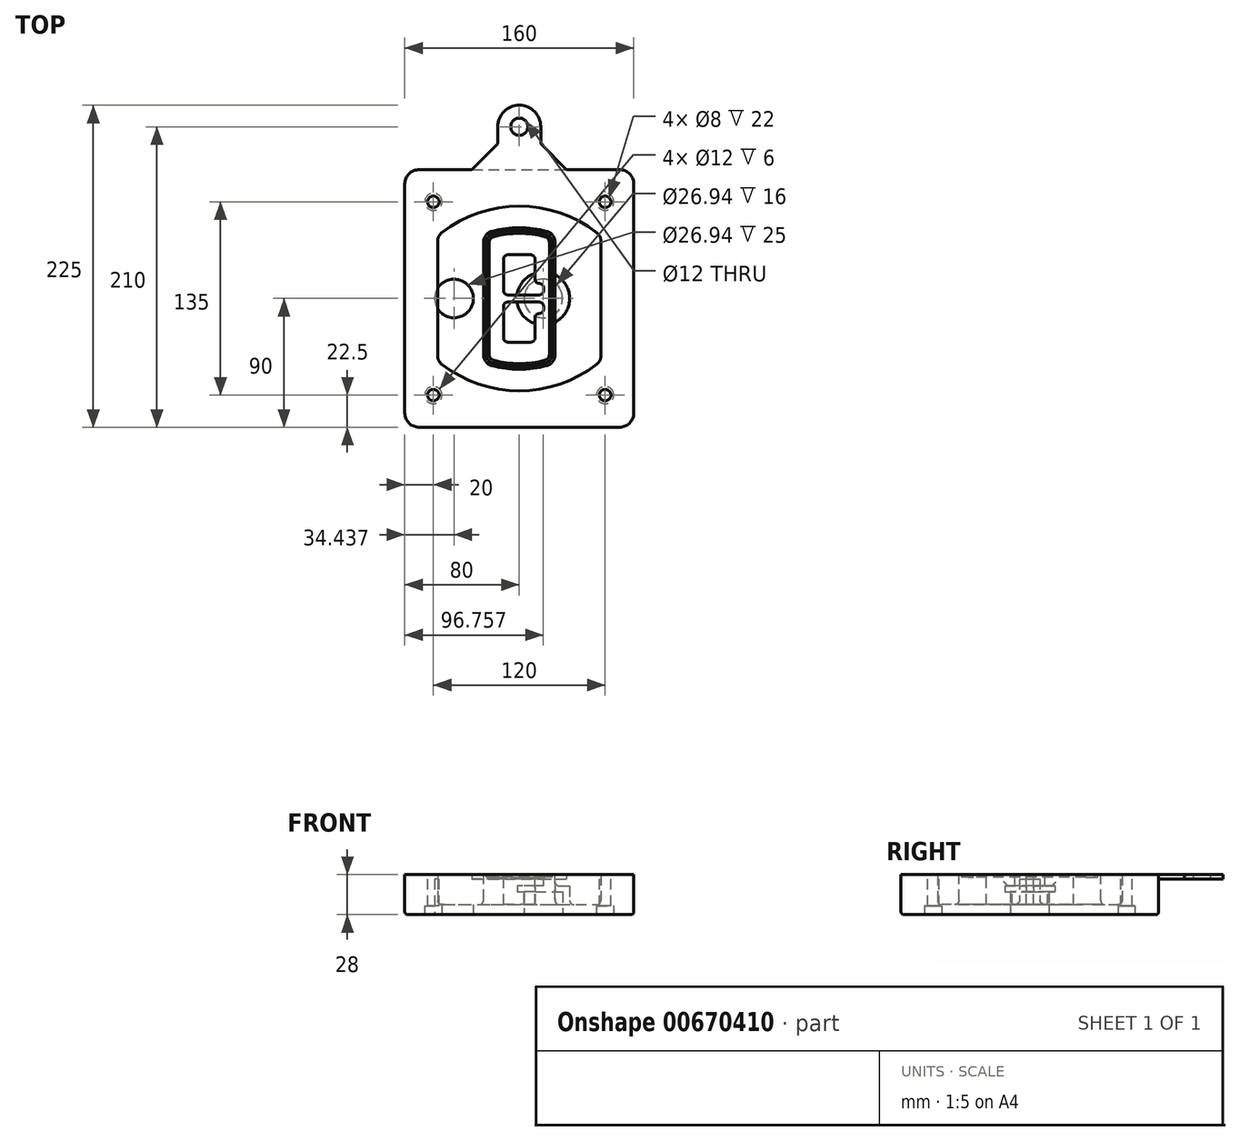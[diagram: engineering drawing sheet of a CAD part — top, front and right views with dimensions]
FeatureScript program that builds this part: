
annotation { "Feature Type Name" : "Feature", "Feature Type Description" : "" }
export const myFeature = defineFeature(function(context is Context, id is Id, definition is map)
    precondition{}
    {
        {
            var Q0;
            Q0=qCreatedBy(makeId("Top.planeOp"),FACE);
            var sketch = newSketch(context, id + "F0", { "sketchPlane" : qUnion([Q0])});
            skPoint(sketch, "E0.rect.middle", {"position": v(0, 0) * mm});
            skLineSegment(sketch, "E1.bottom", {"start": v(-70, -90) * mm, "end": v(70, -90) * mm});
            skLineSegment(sketch, "E1.top", {"start": v(-70, 90) * mm, "end": v(70, 90) * mm});
            skLineSegment(sketch, "E1.left", {"start": v(-80, -80) * mm, "end": v(-80, 80) * mm});
            skLineSegment(sketch, "E1.right", {"start": v(80, -80) * mm, "end": v(80, 80) * mm});
            skLineSegment(sketch, "E2", {"start": v(-80, 90) * mm, "end": v(80, -90) * mm, "construction": true});
            skLineSegment(sketch, "E3", {"start": v(80, 90) * mm, "end": v(-80, -90) * mm, "construction": true});
            skCircle(sketch, "E4", {"center": v(-60, 67.5) * mm, "radius": 4 * mm});
            skCircle(sketch, "E5", {"center": v(60, 67.5) * mm, "radius": 4 * mm});
            skCircle(sketch, "E6", {"center": v(60, -67.5) * mm, "radius": 4 * mm});
            skCircle(sketch, "E7", {"center": v(-60, -67.5) * mm, "radius": 4 * mm});
            skLineSegment(sketch, "E8", {"start": v(-60, 67.5) * mm, "end": v(60, 67.5) * mm, "construction": true});
            skLineSegment(sketch, "E9", {"start": v(60, 67.5) * mm, "end": v(60, -67.5) * mm, "construction": true});
            skLineSegment(sketch, "E10", {"start": v(60, -67.5) * mm, "end": v(-60, -67.5) * mm, "construction": true});
            skLineSegment(sketch, "E11", {"start": v(-60, -67.5) * mm, "end": v(-60, 67.5) * mm, "construction": true});
            skLineSegment(sketch, "E12", {"start": v(-60, 40.3) * mm, "end": v(-60, -40.3) * mm});
            skLineSegment(sketch, "E13", {"start": v(60, 40.3) * mm, "end": v(60, -40.3) * mm});
            skArc(sketch, "E14", {"start": v(56.15, 48.18) * mm, "mid": v(0, 67.5) * mm, "end": v(-56.15, 48.18) * mm});
            skArc(sketch, "E15", {"start": v(-56.15, -48.18) * mm, "mid": v(0, -67.5) * mm, "end": v(56.15, -48.18) * mm});
            skLineSegment(sketch, "E16", {"start": v(-60, 0) * mm, "end": v(60, 0) * mm, "construction": true});
            skPoint(sketch, "E17.visualSharp", {"position": v(-60, -45) * mm});
            skArc(sketch, "E17.filletArc", {"start": v(-60, -40.3) * mm, "mid": v(-58.99, -44.68) * mm, "end": v(-56.15, -48.18) * mm});
            skPoint(sketch, "E18.visualSharp", {"position": v(-60, 45) * mm});
            skArc(sketch, "E18.filletArc", {"start": v(-56.15, 48.18) * mm, "mid": v(-58.99, 44.68) * mm, "end": v(-60, 40.3) * mm});
            skPoint(sketch, "E19.visualSharp", {"position": v(60, 45) * mm});
            skArc(sketch, "E19.filletArc", {"start": v(60, 40.3) * mm, "mid": v(58.99, 44.68) * mm, "end": v(56.15, 48.18) * mm});
            skPoint(sketch, "E20.visualSharp", {"position": v(60, -45) * mm});
            skArc(sketch, "E20.filletArc", {"start": v(56.15, -48.18) * mm, "mid": v(58.99, -44.68) * mm, "end": v(60, -40.3) * mm});
            skPoint(sketch, "E21.visualSharp", {"position": v(-80, 90) * mm});
            skArc(sketch, "E21.filletArc", {"start": v(-70, 90) * mm, "mid": v(-77.07, 87.07) * mm, "end": v(-80, 80) * mm});
            skPoint(sketch, "E22.visualSharp", {"position": v(80, 90) * mm});
            skArc(sketch, "E22.filletArc", {"start": v(80, 80) * mm, "mid": v(77.07, 87.07) * mm, "end": v(70, 90) * mm});
            skPoint(sketch, "E23.visualSharp", {"position": v(80, -90) * mm});
            skArc(sketch, "E23.filletArc", {"start": v(70, -90) * mm, "mid": v(77.07, -87.07) * mm, "end": v(80, -80) * mm});
            skPoint(sketch, "E24.visualSharp", {"position": v(-80, -90) * mm});
            skArc(sketch, "E24.filletArc", {"start": v(-80, -80) * mm, "mid": v(-77.07, -87.07) * mm, "end": v(-70, -90) * mm});
            skArc(sketch, "E25.0", {"start": v(57, 40.3) * mm, "mid": v(56.3, 43.36) * mm, "end": v(54.3, 45.81) * mm});
            skLineSegment(sketch, "E25.1", {"start": v(57, 40.3) * mm, "end": v(57, -40.3) * mm});
            skArc(sketch, "E25.2", {"start": v(54.3, -45.81) * mm, "mid": v(56.3, -43.36) * mm, "end": v(57, -40.3) * mm});
            skArc(sketch, "E25.3", {"start": v(-54.3, -45.81) * mm, "mid": v(0, -64.5) * mm, "end": v(54.3, -45.81) * mm});
            skArc(sketch, "E25.4", {"start": v(-57, -40.3) * mm, "mid": v(-56.3, -43.36) * mm, "end": v(-54.3, -45.81) * mm});
            skArc(sketch, "E25.5", {"start": v(54.3, 45.81) * mm, "mid": v(0, 64.5) * mm, "end": v(-54.3, 45.81) * mm});
            skLineSegment(sketch, "E25.6", {"start": v(-57, 40.3) * mm, "end": v(-57, -40.3) * mm});
            skArc(sketch, "E25.7", {"start": v(-54.3, 45.81) * mm, "mid": v(-56.3, 43.36) * mm, "end": v(-57, 40.3) * mm});
            skArc(sketch, "E26.0", {"start": v(-58.62, 51.33) * mm, "mid": v(-62.58, 46.43) * mm, "end": v(-64, 40.3) * mm});
            skArc(sketch, "E26.1", {"start": v(58.62, 51.33) * mm, "mid": v(0, 71.5) * mm, "end": v(-58.62, 51.33) * mm});
            skArc(sketch, "E26.2", {"start": v(64, 40.3) * mm, "mid": v(62.58, 46.43) * mm, "end": v(58.62, 51.33) * mm});
            skLineSegment(sketch, "E26.3", {"start": v(64, 40.3) * mm, "end": v(64, -40.3) * mm});
            skArc(sketch, "E26.4", {"start": v(58.62, -51.33) * mm, "mid": v(62.58, -46.43) * mm, "end": v(64, -40.3) * mm});
            skLineSegment(sketch, "E26.5", {"start": v(-64, 40.3) * mm, "end": v(-64, -40.3) * mm});
            skArc(sketch, "E26.6", {"start": v(-58.62, -51.33) * mm, "mid": v(0, -71.5) * mm, "end": v(58.62, -51.33) * mm});
            skArc(sketch, "E26.7", {"start": v(-64, -40.3) * mm, "mid": v(-62.58, -46.43) * mm, "end": v(-58.62, -51.33) * mm});
            skSolve(sketch);
        }
        {
            var Q0;
            Q0=makeQuery(id+"F0.imprint","IMPRINT",FACE,{"disambiguationData":[TD([[makeQuery(id+"F0.imprint","IMPRINT",EDGE,{"derivedFrom":sQuery(id+"F0.wireOp",EDGE,"E1.bottom")}),1.0]])]});
            var Q1;
            Q1=makeQuery(id+"F0.imprint","IMPRINT",FACE,{"disambiguationData":[TD([[makeQuery(id+"F0.imprint","IMPRINT",EDGE,{"derivedFrom":sQuery(id+"F0.wireOp",EDGE,"E12")}),1.0]])]});
            var Q2;
            Q2=makeQuery(id+"F0.imprint","IMPRINT",FACE,{"disambiguationData":[TD([[makeQuery(id+"F0.imprint","IMPRINT",EDGE,{"derivedFrom":sQuery(id+"F0.wireOp",EDGE,"E25.0")}),1.0]])]});
            var Q3;
            Q3=makeQuery(id+"F0.imprint","IMPRINT",FACE,{"disambiguationData":[TD([[makeQuery(id+"F0.imprint","IMPRINT",EDGE,{"derivedFrom":sQuery(id+"F0.wireOp",EDGE,"E12")}),-1.0]])]});
            extrude(context, id + "F1", {"entities" : qUnion([Q0, Q1, Q2, Q3]), "oppositeDirection" : true, "depth" : 25 * mm});
        }
        {
            var Q0;
            Q0=makeQuery(id+"F0.imprint","IMPRINT",FACE,{"disambiguationData":[TD([[makeQuery(id+"F0.imprint","IMPRINT",EDGE,{"derivedFrom":sQuery(id+"F0.wireOp",EDGE,"E12")}),1.0]])]});
            extrude(context, id + "F2", {"entities" : qUnion([Q0]), "operationType" : NewBodyOperationType.ADD, "depth" : 3 * mm});
        }
        {
            var Q0;
            Q0=makeQuery(id+"F0.imprint","IMPRINT",FACE,{"disambiguationData":[TD([[makeQuery(id+"F0.imprint","IMPRINT",EDGE,{"derivedFrom":sQuery(id+"F0.wireOp",EDGE,"E25.0")}),1.0]])]});
            extrude(context, id + "F3", {"entities" : qUnion([Q0]), "operationType" : NewBodyOperationType.REMOVE, "oppositeDirection" : true, "depth" : 18 * mm});
        }
        {
            var Q0;
            Q0=makeQuery(id+"F2.opExtrude","CAP_FACE",FACE,{"disambiguationData":[OSD([sQuery(id+"F0.wireOp",EDGE,"E12"),sQuery(id+"F0.wireOp",EDGE,"E13"),sQuery(id+"F0.wireOp",EDGE,"E14"),sQuery(id+"F0.wireOp",EDGE,"E15"),sQuery(id+"F0.wireOp",EDGE,"E17.filletArc"),sQuery(id+"F0.wireOp",EDGE,"E18.filletArc"),sQuery(id+"F0.wireOp",EDGE,"E19.filletArc"),sQuery(id+"F0.wireOp",EDGE,"E20.filletArc"),sQuery(id+"F0.wireOp",EDGE,"E25.0"),sQuery(id+"F0.wireOp",EDGE,"E25.1"),sQuery(id+"F0.wireOp",EDGE,"E25.2"),sQuery(id+"F0.wireOp",EDGE,"E25.3"),sQuery(id+"F0.wireOp",EDGE,"E25.4"),sQuery(id+"F0.wireOp",EDGE,"E25.5"),sQuery(id+"F0.wireOp",EDGE,"E25.6"),sQuery(id+"F0.wireOp",EDGE,"E25.7")])],"isStart":false});
            var sketch = newSketch(context, id + "F4", { "sketchPlane" : qUnion([Q0])});
            skArc(sketch, "E27.0", {"start": v(-19.08, -46.97) * mm, "mid": v(0, -49.5) * mm, "end": v(19.08, -46.97) * mm});
            skArc(sketch, "E28.0", {"start": v(19.08, 46.97) * mm, "mid": v(0, 49.5) * mm, "end": v(-19.08, 46.97) * mm});
            skLineSegment(sketch, "E29", {"start": v(-25, 39.25) * mm, "end": v(-25, -39.25) * mm});
            skLineSegment(sketch, "E30", {"start": v(25, 39.25) * mm, "end": v(25, -39.25) * mm});
            skLineSegment(sketch, "E31", {"start": v(-25, 45.1) * mm, "end": v(25, 45.1) * mm, "construction": true});
            skLineSegment(sketch, "E32", {"start": v(-25, -45.1) * mm, "end": v(25, -45.1) * mm, "construction": true});
            skPoint(sketch, "E33.visualSharp", {"position": v(-25, 45.1) * mm});
            skArc(sketch, "E33.filletArc", {"start": v(-19.08, 46.97) * mm, "mid": v(-23.35, 44.11) * mm, "end": v(-25, 39.25) * mm});
            skPoint(sketch, "E34.visualSharp", {"position": v(25, 45.1) * mm});
            skArc(sketch, "E34.filletArc", {"start": v(25, 39.25) * mm, "mid": v(23.35, 44.11) * mm, "end": v(19.08, 46.97) * mm});
            skPoint(sketch, "E35.visualSharp", {"position": v(25, -45.1) * mm});
            skArc(sketch, "E35.filletArc", {"start": v(19.08, -46.97) * mm, "mid": v(23.35, -44.11) * mm, "end": v(25, -39.25) * mm});
            skPoint(sketch, "E36.visualSharp", {"position": v(-25, -45.1) * mm});
            skArc(sketch, "E36.filletArc", {"start": v(-25, -39.25) * mm, "mid": v(-23.35, -44.11) * mm, "end": v(-19.08, -46.97) * mm});
            skArc(sketch, "E37.0", {"start": v(54.3, 45.81) * mm, "mid": v(0, 64.5) * mm, "end": v(-54.3, 45.81) * mm});
            skArc(sketch, "E37.1", {"start": v(-54.3, 45.81) * mm, "mid": v(-56.3, 43.36) * mm, "end": v(-57, 40.3) * mm});
            skLineSegment(sketch, "E37.2", {"start": v(-57, 40.3) * mm, "end": v(-57, -40.3) * mm});
            skArc(sketch, "E37.3", {"start": v(-57, -40.3) * mm, "mid": v(-56.3, -43.36) * mm, "end": v(-54.3, -45.81) * mm});
            skArc(sketch, "E37.4", {"start": v(-54.3, -45.81) * mm, "mid": v(0, -64.5) * mm, "end": v(54.3, -45.81) * mm});
            skArc(sketch, "E37.5", {"start": v(54.3, -45.81) * mm, "mid": v(56.3, -43.36) * mm, "end": v(57, -40.3) * mm});
            skLineSegment(sketch, "E37.6", {"start": v(57, 40.3) * mm, "end": v(57, -40.3) * mm});
            skArc(sketch, "E37.7", {"start": v(57, 40.3) * mm, "mid": v(56.3, 43.36) * mm, "end": v(54.3, 45.81) * mm});
            skLineSegment(sketch, "E38.0", {"start": v(23, 39.25) * mm, "end": v(23, -39.25) * mm});
            skArc(sketch, "E38.1", {"start": v(18.56, -45.04) * mm, "mid": v(21.76, -42.9) * mm, "end": v(23, -39.25) * mm});
            skArc(sketch, "E38.2", {"start": v(-18.56, -45.04) * mm, "mid": v(0, -47.5) * mm, "end": v(18.56, -45.04) * mm});
            skArc(sketch, "E38.3", {"start": v(-23, -39.25) * mm, "mid": v(-21.76, -42.9) * mm, "end": v(-18.56, -45.04) * mm});
            skLineSegment(sketch, "E38.4", {"start": v(-23, 39.25) * mm, "end": v(-23, -39.25) * mm});
            skArc(sketch, "E38.5", {"start": v(23, 39.25) * mm, "mid": v(21.76, 42.9) * mm, "end": v(18.56, 45.04) * mm});
            skArc(sketch, "E38.6", {"start": v(-18.56, 45.04) * mm, "mid": v(-21.76, 42.9) * mm, "end": v(-23, 39.25) * mm});
            skArc(sketch, "E38.7", {"start": v(18.56, 45.04) * mm, "mid": v(0, 47.5) * mm, "end": v(-18.56, 45.04) * mm});
            skArc(sketch, "E39.0", {"start": v(21, 39.25) * mm, "mid": v(20.18, 41.68) * mm, "end": v(18.04, 43.1) * mm});
            skLineSegment(sketch, "E39.1", {"start": v(21, 39.25) * mm, "end": v(21, -39.25) * mm});
            skArc(sketch, "E39.2", {"start": v(18.04, -43.1) * mm, "mid": v(20.18, -41.68) * mm, "end": v(21, -39.25) * mm});
            skArc(sketch, "E39.3", {"start": v(-18.04, -43.1) * mm, "mid": v(0, -45.5) * mm, "end": v(18.04, -43.1) * mm});
            skArc(sketch, "E39.4", {"start": v(-21, -39.25) * mm, "mid": v(-20.18, -41.68) * mm, "end": v(-18.04, -43.1) * mm});
            skArc(sketch, "E39.5", {"start": v(18.04, 43.1) * mm, "mid": v(0, 45.5) * mm, "end": v(-18.04, 43.1) * mm});
            skLineSegment(sketch, "E39.6", {"start": v(-21, 39.25) * mm, "end": v(-21, -39.25) * mm});
            skArc(sketch, "E39.7", {"start": v(-18.04, 43.1) * mm, "mid": v(-20.18, 41.68) * mm, "end": v(-21, 39.25) * mm});
            skLineSegment(sketch, "E40", {"start": v(-25, 0) * mm, "end": v(25, 0) * mm, "construction": true});
            skLineSegment(sketch, "E41", {"start": v(-11, 5.5) * mm, "end": v(-11, 27.5) * mm});
            skLineSegment(sketch, "E42", {"start": v(-8, 30.5) * mm, "end": v(8, 30.5) * mm});
            skLineSegment(sketch, "E43", {"start": v(11, 27.5) * mm, "end": v(11, 13.5) * mm});
            skLineSegment(sketch, "E44", {"start": v(14, 10.5) * mm, "end": v(14, 10.5) * mm});
            skLineSegment(sketch, "E45", {"start": v(17, 7.5) * mm, "end": v(17, 5.5) * mm});
            skLineSegment(sketch, "E46", {"start": v(14, 2.5) * mm, "end": v(-8, 2.5) * mm});
            skPoint(sketch, "E47.visualSharp", {"position": v(-11, 30.5) * mm});
            skArc(sketch, "E47.filletArc", {"start": v(-8, 30.5) * mm, "mid": v(-10.12, 29.62) * mm, "end": v(-11, 27.5) * mm});
            skPoint(sketch, "E48.visualSharp", {"position": v(11, 30.5) * mm});
            skArc(sketch, "E48.filletArc", {"start": v(11, 27.5) * mm, "mid": v(10.12, 29.62) * mm, "end": v(8, 30.5) * mm});
            skPoint(sketch, "E49.visualSharp", {"position": v(11, 10.5) * mm});
            skArc(sketch, "E49.filletArc", {"start": v(11, 13.5) * mm, "mid": v(11.88, 11.38) * mm, "end": v(14, 10.5) * mm});
            skPoint(sketch, "E50.visualSharp", {"position": v(17, 10.5) * mm});
            skArc(sketch, "E50.filletArc", {"start": v(17, 7.5) * mm, "mid": v(16.12, 9.62) * mm, "end": v(14, 10.5) * mm});
            skPoint(sketch, "E51.visualSharp", {"position": v(17, 2.5) * mm});
            skArc(sketch, "E51.filletArc", {"start": v(14, 2.5) * mm, "mid": v(16.12, 3.38) * mm, "end": v(17, 5.5) * mm});
            skPoint(sketch, "E52.visualSharp", {"position": v(-11, 2.5) * mm});
            skArc(sketch, "E52.filletArc", {"start": v(-11, 5.5) * mm, "mid": v(-10.12, 3.38) * mm, "end": v(-8, 2.5) * mm});
            skLineSegment(sketch, "E53.0.MirrorCS", {"start": v(14, -2.5) * mm, "end": v(-8, -2.5) * mm});
            skArc(sketch, "E54.0.MirrorCS", {"start": v(-11, -5.5) * mm, "mid": v(-10.12, -3.38) * mm, "end": v(-8, -2.5) * mm});
            skLineSegment(sketch, "E55.0.MirrorCS", {"start": v(-11, -5.5) * mm, "end": v(-11, -27.5) * mm});
            skArc(sketch, "E56.0.MirrorCS", {"start": v(-8, -30.5) * mm, "mid": v(-10.12, -29.62) * mm, "end": v(-11, -27.5) * mm});
            skLineSegment(sketch, "E57.0.MirrorCS", {"start": v(-8, -30.5) * mm, "end": v(8, -30.5) * mm});
            skArc(sketch, "E58.0.MirrorCS", {"start": v(11, -27.5) * mm, "mid": v(10.12, -29.62) * mm, "end": v(8, -30.5) * mm});
            skLineSegment(sketch, "E59.0.MirrorCS", {"start": v(11, -27.5) * mm, "end": v(11, -13.5) * mm});
            skArc(sketch, "E60.0.MirrorCS", {"start": v(11, -13.5) * mm, "mid": v(11.88, -11.38) * mm, "end": v(14, -10.5) * mm});
            skArc(sketch, "E61.0.MirrorCS", {"start": v(17, -7.5) * mm, "mid": v(16.12, -9.62) * mm, "end": v(14, -10.5) * mm});
            skLineSegment(sketch, "E62.0.MirrorCS", {"start": v(17, -7.5) * mm, "end": v(17, -5.5) * mm});
            skArc(sketch, "E63.0.MirrorCS", {"start": v(14, -2.5) * mm, "mid": v(16.12, -3.38) * mm, "end": v(17, -5.5) * mm});
            skSolve(sketch);
        }
        {
            var Q0;
            Q0=makeQuery(id+"F4.imprint","IMPRINT",FACE,{"disambiguationData":[TD([[makeQuery(id+"F4.imprint","IMPRINT",EDGE,{"derivedFrom":sQuery(id+"F4.wireOp",EDGE,"E27.0")}),1.0]])]});
            var Q1;
            Q1=makeQuery(id+"F4.imprint","IMPRINT",FACE,{"disambiguationData":[TD([[makeQuery(id+"F4.imprint","IMPRINT",EDGE,{"derivedFrom":sQuery(id+"F4.wireOp",EDGE,"E38.0")}),-1.0]])]});
            var Q2;
            Q2=makeQuery(id+"F4.imprint","IMPRINT",FACE,{"disambiguationData":[TD([[makeQuery(id+"F4.imprint","IMPRINT",EDGE,{"derivedFrom":sQuery(id+"F4.wireOp",EDGE,"E39.0")}),1.0]])]});
            extrude(context, id + "F5", {"entities" : qUnion([Q0, Q1, Q2]), "operationType" : NewBodyOperationType.ADD, "endBound" : BoundingType.UP_TO_NEXT, "oppositeDirection" : true, "depth" : 25 * mm});
        }
        {
            var Q0;
            Q0=makeQuery(id+"F4.imprint","IMPRINT",FACE,{"disambiguationData":[TD([[makeQuery(id+"F4.imprint","IMPRINT",EDGE,{"derivedFrom":sQuery(id+"F4.wireOp",EDGE,"E38.0")}),-1.0]])]});
            extrude(context, id + "F6", {"entities" : qUnion([Q0]), "operationType" : NewBodyOperationType.REMOVE, "oppositeDirection" : true, "depth" : 2 * mm});
        }
        {
            var Q0;
            Q0=makeQuery(id+"F1.opExtrude","CAP_FACE",FACE,{"disambiguationData":[OSD([sQuery(id+"F0.wireOp",EDGE,"E1.bottom"),sQuery(id+"F0.wireOp",EDGE,"E1.top"),sQuery(id+"F0.wireOp",EDGE,"E1.left"),sQuery(id+"F0.wireOp",EDGE,"E1.right"),sQuery(id+"F0.wireOp",EDGE,"E4"),sQuery(id+"F0.wireOp",EDGE,"E5"),sQuery(id+"F0.wireOp",EDGE,"E6"),sQuery(id+"F0.wireOp",EDGE,"E7"),sQuery(id+"F0.wireOp",EDGE,"E21.filletArc"),sQuery(id+"F0.wireOp",EDGE,"E22.filletArc"),sQuery(id+"F0.wireOp",EDGE,"E23.filletArc"),sQuery(id+"F0.wireOp",EDGE,"E24.filletArc")])],"isStart":false});
            var sketch = newSketch(context, id + "F7", { "sketchPlane" : qUnion([Q0])});
            skCircle(sketch, "E64", {"center": v(16.76, 0) * mm, "radius": 13.47 * mm});
            skCircle(sketch, "E65", {"center": v(-45.56, 0) * mm, "radius": 13.47 * mm});
            skLineSegment(sketch, "E66", {"start": v(80, 0) * mm, "end": v(-80, 0) * mm});
            skCircle(sketch, "E67", {"center": v(16.76, 0) * mm, "radius": 18.47 * mm});
            skCircle(sketch, "E68", {"center": v(60, -67.5) * mm, "radius": 6 * mm});
            skCircle(sketch, "E69", {"center": v(-60, -67.5) * mm, "radius": 6 * mm});
            skCircle(sketch, "E70", {"center": v(-60, 67.5) * mm, "radius": 6 * mm});
            skCircle(sketch, "E71", {"center": v(60, 67.5) * mm, "radius": 6 * mm});
            skSolve(sketch);
        }
        {
            var Q0;
            {var subQ1=sQuery(id+"F7.wireOp",EDGE,"E66");var subQ4=sQuery(id+"F7.wireOp",EDGE,"E64");var subQ6=makeQuery(id+"F7.imprint","INTERSECT",VERTEX,{"disambiguationData":[OD(0.0)],"derivedFrom":[subQ4,subQ1]});Q0=makeQuery(id+"F7.imprint","IMPRINT",FACE,{"disambiguationData":[TD([[makeQuery(id+"F7.imprint","IMPRINT",EDGE,{"disambiguationData":[TD([[subQ6,-1.0]])],"derivedFrom":subQ4}),-1.0]])]});}
            var Q1;
            {var subQ0=sQuery(id+"F7.wireOp",EDGE,"E66");var subQ1=sQuery(id+"F7.wireOp",EDGE,"E64");var subQ3=makeQuery(id+"F7.imprint","INTERSECT",VERTEX,{"disambiguationData":[OD(0.0)],"derivedFrom":[subQ1,subQ0]});Q1=makeQuery(id+"F7.imprint","IMPRINT",FACE,{"disambiguationData":[TD([[makeQuery(id+"F7.imprint","IMPRINT",EDGE,{"disambiguationData":[TD([[subQ3,-1.0]])],"derivedFrom":subQ1}),1.0]])]});}
            var Q2;
            {var subQ0=sQuery(id+"F7.wireOp",EDGE,"E66");var subQ1=sQuery(id+"F7.wireOp",EDGE,"E64");var subQ3=makeQuery(id+"F7.imprint","INTERSECT",VERTEX,{"disambiguationData":[OD(0.0)],"derivedFrom":[subQ1,subQ0]});Q2=makeQuery(id+"F7.imprint","IMPRINT",FACE,{"disambiguationData":[TD([[makeQuery(id+"F7.imprint","IMPRINT",EDGE,{"disambiguationData":[TD([[subQ3,1.0]])],"derivedFrom":subQ1}),1.0]])]});}
            var Q3;
            {var subQ1=sQuery(id+"F7.wireOp",EDGE,"E66");var subQ4=sQuery(id+"F7.wireOp",EDGE,"E64");var subQ6=makeQuery(id+"F7.imprint","INTERSECT",VERTEX,{"disambiguationData":[OD(0.0)],"derivedFrom":[subQ4,subQ1]});Q3=makeQuery(id+"F7.imprint","IMPRINT",FACE,{"disambiguationData":[TD([[makeQuery(id+"F7.imprint","IMPRINT",EDGE,{"disambiguationData":[TD([[subQ6,1.0]])],"derivedFrom":subQ4}),-1.0]])]});}
            extrude(context, id + "F8", {"entities" : qUnion([Q0, Q1, Q2, Q3]), "operationType" : NewBodyOperationType.ADD, "oppositeDirection" : true, "depth" : 20 * mm});
        }
        {
            var Q0;
            {var subQ0=sQuery(id+"F7.wireOp",EDGE,"E66");var subQ1=sQuery(id+"F7.wireOp",EDGE,"E64");var subQ3=makeQuery(id+"F7.imprint","INTERSECT",VERTEX,{"disambiguationData":[OD(0.0)],"derivedFrom":[subQ1,subQ0]});Q0=makeQuery(id+"F7.imprint","IMPRINT",FACE,{"disambiguationData":[TD([[makeQuery(id+"F7.imprint","IMPRINT",EDGE,{"disambiguationData":[TD([[subQ3,-1.0]])],"derivedFrom":subQ1}),1.0]])]});}
            var Q1;
            {var subQ0=sQuery(id+"F7.wireOp",EDGE,"E66");var subQ1=sQuery(id+"F7.wireOp",EDGE,"E64");var subQ3=makeQuery(id+"F7.imprint","INTERSECT",VERTEX,{"disambiguationData":[OD(0.0)],"derivedFrom":[subQ1,subQ0]});Q1=makeQuery(id+"F7.imprint","IMPRINT",FACE,{"disambiguationData":[TD([[makeQuery(id+"F7.imprint","IMPRINT",EDGE,{"disambiguationData":[TD([[subQ3,1.0]])],"derivedFrom":subQ1}),1.0]])]});}
            extrude(context, id + "F9", {"entities" : qUnion([Q0, Q1]), "operationType" : NewBodyOperationType.REMOVE, "oppositeDirection" : true, "depth" : 16 * mm});
        }
        {
            var Q0;
            {var subQ0=sQuery(id+"F7.wireOp",EDGE,"E66");var subQ1=sQuery(id+"F7.wireOp",EDGE,"E65");var subQ3=makeQuery(id+"F7.imprint","INTERSECT",VERTEX,{"disambiguationData":[OD(0.0)],"derivedFrom":[subQ1,subQ0]});Q0=makeQuery(id+"F7.imprint","IMPRINT",FACE,{"disambiguationData":[TD([[makeQuery(id+"F7.imprint","IMPRINT",EDGE,{"disambiguationData":[TD([[subQ3,-1.0]])],"derivedFrom":subQ1}),1.0]])]});}
            var Q1;
            {var subQ0=sQuery(id+"F7.wireOp",EDGE,"E66");var subQ1=sQuery(id+"F7.wireOp",EDGE,"E65");var subQ3=makeQuery(id+"F7.imprint","INTERSECT",VERTEX,{"disambiguationData":[OD(0.0)],"derivedFrom":[subQ1,subQ0]});Q1=makeQuery(id+"F7.imprint","IMPRINT",FACE,{"disambiguationData":[TD([[makeQuery(id+"F7.imprint","IMPRINT",EDGE,{"disambiguationData":[TD([[subQ3,1.0]])],"derivedFrom":subQ1}),1.0]])]});}
            extrude(context, id + "F10", {"entities" : qUnion([Q0, Q1]), "operationType" : NewBodyOperationType.REMOVE, "oppositeDirection" : true, "depth" : 25 * mm});
        }
        {
            var Q0;
            Q0=makeQuery(id+"F7.imprint","IMPRINT",FACE,{"disambiguationData":[TD([[makeQuery(id+"F7.imprint","IMPRINT",EDGE,{"derivedFrom":sQuery(id+"F7.wireOp",EDGE,"E68")}),1.0]])]});
            var Q1;
            Q1=makeQuery(id+"F7.imprint","IMPRINT",FACE,{"disambiguationData":[TD([[makeQuery(id+"F7.imprint","IMPRINT",EDGE,{"derivedFrom":makeQuery(id+"F1.opExtrude","CAP_EDGE",EDGE,{"disambiguationData":[OSD([sQuery(id+"F0.wireOp",EDGE,"E5")])],"isStart":false})}),-1.0]])]});
            var Q2;
            Q2=makeQuery(id+"F7.imprint","IMPRINT",FACE,{"disambiguationData":[TD([[makeQuery(id+"F7.imprint","IMPRINT",EDGE,{"derivedFrom":sQuery(id+"F7.wireOp",EDGE,"E69")}),1.0]])]});
            var Q3;
            Q3=makeQuery(id+"F7.imprint","IMPRINT",FACE,{"disambiguationData":[TD([[makeQuery(id+"F7.imprint","IMPRINT",EDGE,{"derivedFrom":makeQuery(id+"F1.opExtrude","CAP_EDGE",EDGE,{"disambiguationData":[OSD([sQuery(id+"F0.wireOp",EDGE,"E4")])],"isStart":false})}),-1.0]])]});
            var Q4;
            Q4=makeQuery(id+"F7.imprint","IMPRINT",FACE,{"disambiguationData":[TD([[makeQuery(id+"F7.imprint","IMPRINT",EDGE,{"derivedFrom":sQuery(id+"F7.wireOp",EDGE,"E70")}),1.0]])]});
            var Q5;
            Q5=makeQuery(id+"F7.imprint","IMPRINT",FACE,{"disambiguationData":[TD([[makeQuery(id+"F7.imprint","IMPRINT",EDGE,{"derivedFrom":makeQuery(id+"F1.opExtrude","CAP_EDGE",EDGE,{"disambiguationData":[OSD([sQuery(id+"F0.wireOp",EDGE,"E7")])],"isStart":false})}),-1.0]])]});
            var Q6;
            Q6=makeQuery(id+"F7.imprint","IMPRINT",FACE,{"disambiguationData":[TD([[makeQuery(id+"F7.imprint","IMPRINT",EDGE,{"derivedFrom":sQuery(id+"F7.wireOp",EDGE,"E71")}),1.0]])]});
            var Q7;
            Q7=makeQuery(id+"F7.imprint","IMPRINT",FACE,{"disambiguationData":[TD([[makeQuery(id+"F7.imprint","IMPRINT",EDGE,{"derivedFrom":makeQuery(id+"F1.opExtrude","CAP_EDGE",EDGE,{"disambiguationData":[OSD([sQuery(id+"F0.wireOp",EDGE,"E6")])],"isStart":false})}),-1.0]])]});
            extrude(context, id + "F11", {"entities" : qUnion([Q0, Q1, Q2, Q3, Q4, Q5, Q6, Q7]), "operationType" : NewBodyOperationType.REMOVE, "oppositeDirection" : true, "depth" : 6 * mm});
        }
        {
            var Q0;
            Q0=makeQuery(id+"F9.boolean.opBoolean","COPY",FACE,{"derivedFrom":makeQuery(id+"F9.opExtrude","CAP_FACE",FACE,{"disambiguationData":[OSD([sQuery(id+"F7.wireOp",EDGE,"E64")])],"isStart":false})});
            var sketch = newSketch(context, id + "F12", { "sketchPlane" : qUnion([Q0])});
            skArc(sketch, "E72.0", {"start": v(11, 17.55) * mm, "mid": v(2.57, 11.82) * mm, "end": v(-1.54, 2.5) * mm});
            skArc(sketch, "E72.1", {"start": v(-1.54, -2.5) * mm, "mid": v(2.57, -11.82) * mm, "end": v(11, -17.55) * mm});
            skLineSegment(sketch, "E73", {"start": v(-1.54, -2.5) * mm, "end": v(14, -2.5) * mm});
            skLineSegment(sketch, "E74.0", {"start": v(14, 2.5) * mm, "end": v(-1.54, 2.5) * mm});
            skArc(sketch, "E74.1", {"start": v(14, 2.5) * mm, "mid": v(16.12, 3.38) * mm, "end": v(17, 5.5) * mm});
            skLineSegment(sketch, "E74.2", {"start": v(17, 7.5) * mm, "end": v(17, 5.5) * mm});
            skArc(sketch, "E74.3", {"start": v(17, 7.5) * mm, "mid": v(16.12, 9.62) * mm, "end": v(14, 10.5) * mm});
            skArc(sketch, "E74.4", {"start": v(11, 13.5) * mm, "mid": v(11.88, 11.38) * mm, "end": v(14, 10.5) * mm});
            skLineSegment(sketch, "E74.5", {"start": v(11, 17.55) * mm, "end": v(11, 13.5) * mm});
            skLineSegment(sketch, "E74.7", {"start": v(14, -2.5) * mm, "end": v(-1.54, -2.5) * mm});
            skArc(sketch, "E74.8", {"start": v(14, -2.5) * mm, "mid": v(16.12, -3.38) * mm, "end": v(17, -5.5) * mm});
            skLineSegment(sketch, "E74.9", {"start": v(17, -7.5) * mm, "end": v(17, -5.5) * mm});
            skArc(sketch, "E74.10", {"start": v(17, -7.5) * mm, "mid": v(16.12, -9.62) * mm, "end": v(14, -10.5) * mm});
            skArc(sketch, "E74.11", {"start": v(11, -13.5) * mm, "mid": v(11.88, -11.38) * mm, "end": v(14, -10.5) * mm});
            skLineSegment(sketch, "E74.12", {"start": v(11, -17.55) * mm, "end": v(11, -13.5) * mm});
            skPoint(sketch, "E75.orphan", {"position": v(11, -27.5) * mm});
            skPoint(sketch, "E76.orphan", {"position": v(-8, -2.5) * mm});
            skPoint(sketch, "E77.orphan", {"position": v(-8, 2.5) * mm});
            skPoint(sketch, "E78.orphan", {"position": v(11, 27.5) * mm});
            skSolve(sketch);
        }
        {
            var Q0;
            {var subQ7=sQuery(id+"F12.wireOp",EDGE,"E72.0");var subQ14=sQuery(id+"F12.wireOp",EDGE,"E72.1");var subQ16=sQuery(id+"F12.wireOp",EDGE,"E74.1");var subQ18=sQuery(id+"F12.wireOp",EDGE,"E74.8");Q0=qUnion([makeQuery(id+"F12.imprint","IMPRINT",FACE,{"disambiguationData":[TD([[makeQuery(id+"F12.imprint","IMPRINT",EDGE,{"derivedFrom":subQ7}),1.0]])]}),makeQuery(id+"F12.imprint","IMPRINT",FACE,{"disambiguationData":[TD([[makeQuery(id+"F12.imprint","IMPRINT",EDGE,{"derivedFrom":subQ14}),1.0]])]}),makeQuery(id+"F12.imprint","IMPRINT",FACE,{"disambiguationData":[TD([[makeQuery(id+"F12.imprint","IMPRINT",EDGE,{"derivedFrom":subQ16}),1.0]])]}),makeQuery(id+"F12.imprint","IMPRINT",FACE,{"disambiguationData":[TD([[makeQuery(id+"F12.imprint","IMPRINT",EDGE,{"derivedFrom":subQ18}),-1.0]])]})]);}
            var Q1;
            Q1=makeQuery(id+"F5.boolean.opBoolean","SPLIT",FACE,{"disambiguationData":[TD([makeQuery(id+"F5.opExtrude","SWEPT_FACE",FACE,{"disambiguationData":[OSD([sQuery(id+"F4.wireOp",EDGE,"E41")])]})])],"derivedFrom":makeQuery(id+"F3.boolean.opBoolean","COPY",FACE,{"derivedFrom":makeQuery(id+"F3.opExtrude","CAP_FACE",FACE,{"disambiguationData":[OSD([sQuery(id+"F0.wireOp",EDGE,"E25.0"),sQuery(id+"F0.wireOp",EDGE,"E25.1"),sQuery(id+"F0.wireOp",EDGE,"E25.2"),sQuery(id+"F0.wireOp",EDGE,"E25.3"),sQuery(id+"F0.wireOp",EDGE,"E25.4"),sQuery(id+"F0.wireOp",EDGE,"E25.5"),sQuery(id+"F0.wireOp",EDGE,"E25.6"),sQuery(id+"F0.wireOp",EDGE,"E25.7")])],"isStart":false})})});
            extrude(context, id + "F13", {"entities" : qUnion([Q0]), "operationType" : NewBodyOperationType.REMOVE, "endBound" : BoundingType.UP_TO_SURFACE, "endBoundEntityFace" : qUnion([Q1]), "depth" : 25 * mm});
        }
        {
            var Q0;
            Q0=makeQuery(id+"F3.boolean.opBoolean","COPY",EDGE,{"derivedFrom":makeQuery(id+"F3.opExtrude","CAP_EDGE",EDGE,{"disambiguationData":[OSD([sQuery(id+"F0.wireOp",EDGE,"E25.6")])],"isStart":false})});
            var Q1;
            Q1=makeQuery(id+"F8.boolean.opBoolean","INTERSECT",EDGE,{"derivedFrom":[makeQuery(id+"F5.opExtrude","SWEPT_FACE",FACE,{"disambiguationData":[OSD([sQuery(id+"F4.wireOp",EDGE,"E30")])]}),makeQuery(id+"F8.opExtrude","CAP_FACE",FACE,{"disambiguationData":[OSD([sQuery(id+"F7.wireOp",EDGE,"E67")])],"isStart":false})]});
            var Q2;
            Q2=makeQuery(id+"F8.boolean.opBoolean","INTERSECT",EDGE,{"disambiguationData":[OD(1.0)],"derivedFrom":[makeQuery(id+"F5.opExtrude","SWEPT_FACE",FACE,{"disambiguationData":[OSD([sQuery(id+"F4.wireOp",EDGE,"E30")])]}),makeQuery(id+"F8.opExtrude","SWEPT_FACE",FACE,{"disambiguationData":[OSD([sQuery(id+"F7.wireOp",EDGE,"E67")])]})]});
            var Q3;
            {var subQ0=sQuery(id+"F4.wireOp",EDGE,"E30");Q3=makeQuery(id+"F8.boolean.opBoolean","SPLIT",EDGE,{"disambiguationData":[TD([makeQuery(id+"F5.opExtrude","SWEPT_FACE",FACE,{"disambiguationData":[OSD([sQuery(id+"F4.wireOp",EDGE,"E35.filletArc")])]})])],"derivedFrom":makeQuery(id+"F5.opExtrude","CAP_EDGE",EDGE,{"disambiguationData":[OSD([subQ0])],"isStart":false})});}
            var Q4;
            {var subQ0=sQuery(id+"F0.wireOp",EDGE,"E25.7");var subQ1=sQuery(id+"F0.wireOp",EDGE,"E25.1");var subQ2=sQuery(id+"F0.wireOp",EDGE,"E25.6");var subQ3=sQuery(id+"F0.wireOp",EDGE,"E25.5");var subQ4=sQuery(id+"F0.wireOp",EDGE,"E25.4");var subQ5=sQuery(id+"F0.wireOp",EDGE,"E25.0");var subQ6=sQuery(id+"F0.wireOp",EDGE,"E25.2");var subQ7=sQuery(id+"F0.wireOp",EDGE,"E25.3");Q4=makeQuery(id+"F8.boolean.opBoolean","INTERSECT",EDGE,{"derivedFrom":[makeQuery(id+"F5.boolean.opBoolean","SPLIT",FACE,{"disambiguationData":[TD([makeQuery(id+"F2.opExtrude","SWEPT_FACE",FACE,{"disambiguationData":[OSD([subQ5])]})])],"derivedFrom":makeQuery(id+"F3.boolean.opBoolean","COPY",FACE,{"derivedFrom":makeQuery(id+"F3.opExtrude","CAP_FACE",FACE,{"disambiguationData":[OSD([subQ5,subQ1,subQ6,subQ7,subQ4,subQ3,subQ2,subQ0])],"isStart":false})})}),makeQuery(id+"F8.opExtrude","SWEPT_FACE",FACE,{"disambiguationData":[OSD([sQuery(id+"F7.wireOp",EDGE,"E67")])]})]});}
            var Q5;
            Q5=makeQuery(id+"F8.boolean.opBoolean","INTERSECT",EDGE,{"disambiguationData":[OD(0.0)],"derivedFrom":[makeQuery(id+"F5.opExtrude","SWEPT_FACE",FACE,{"disambiguationData":[OSD([sQuery(id+"F4.wireOp",EDGE,"E30")])]}),makeQuery(id+"F8.opExtrude","SWEPT_FACE",FACE,{"disambiguationData":[OSD([sQuery(id+"F7.wireOp",EDGE,"E67")])]})]});
            fillet(context, id + "F14", {"entities" : qUnion([Q0, Q1, Q2, Q3, Q4, Q5]), "radius" : 3 * mm, "tangentPropagation" : true, "allowEdgeOverflow" : false});
        }
        {
            var Q0;
            Q0=makeQuery(id+"F1.opExtrude","CAP_EDGE",EDGE,{"disambiguationData":[OSD([sQuery(id+"F0.wireOp",EDGE,"E1.bottom")])],"isStart":false});
            fillet(context, id + "F15", {"entities" : qUnion([Q0]), "radius" : 2 * mm, "tangentPropagation" : true, "allowEdgeOverflow" : false});
        }
        {
            var Q0;
            {var subQ0=sQuery(id+"F0.wireOp",EDGE,"E21.filletArc");var subQ1=sQuery(id+"F0.wireOp",EDGE,"E7");var subQ2=sQuery(id+"F0.wireOp",EDGE,"E6");var subQ3=sQuery(id+"F0.wireOp",EDGE,"E5");var subQ4=sQuery(id+"F0.wireOp",EDGE,"E4");var subQ5=sQuery(id+"F0.wireOp",EDGE,"E22.filletArc");var subQ6=sQuery(id+"F0.wireOp",EDGE,"E1.bottom");var subQ7=sQuery(id+"F0.wireOp",EDGE,"E1.right");var subQ8=sQuery(id+"F0.wireOp",EDGE,"E1.top");var subQ9=sQuery(id+"F0.wireOp",EDGE,"E1.left");var subQ10=sQuery(id+"F0.wireOp",EDGE,"E23.filletArc");var subQ11=sQuery(id+"F0.wireOp",EDGE,"E24.filletArc");Q0=makeQuery(id+"F2.boolean.opBoolean","SPLIT",FACE,{"disambiguationData":[TD([makeQuery(id+"F1.opExtrude","SWEPT_FACE",FACE,{"disambiguationData":[OSD([subQ6])]})])],"derivedFrom":makeQuery(id+"F1.opExtrude","CAP_FACE",FACE,{"disambiguationData":[OSD([subQ6,subQ8,subQ9,subQ7,subQ4,subQ3,subQ2,subQ1,subQ0,subQ5,subQ10,subQ11])],"isStart":true})});}
            var sketch = newSketch(context, id + "F16", { "sketchPlane" : qUnion([Q0])});
            skLineSegment(sketch, "E79", {"start": v(0, 90) * mm, "end": v(0, 120) * mm, "construction": true});
            skCircle(sketch, "E80", {"center": v(0, 120) * mm, "radius": 6 * mm});
            skArc(sketch, "E81", {"start": v(15, 120) * mm, "mid": v(0, 135) * mm, "end": v(-15, 120) * mm});
            skLineSegment(sketch, "E82", {"start": v(-15, 120) * mm, "end": v(-15, 108) * mm});
            skLineSegment(sketch, "E83", {"start": v(15, 120) * mm, "end": v(15, 108) * mm});
            skLineSegment(sketch, "E84", {"start": v(15, 108) * mm, "end": v(33, 90) * mm});
            skLineSegment(sketch, "E85", {"start": v(-15, 108) * mm, "end": v(-33, 90) * mm});
            skLineSegment(sketch, "E86", {"start": v(80, 0) * mm, "end": v(-80, 0) * mm, "construction": true});
            skLineSegment(sketch, "E87.MirrorCS", {"start": v(-15, -108) * mm, "end": v(-33, -90) * mm});
            skArc(sketch, "E88.MirrorCS", {"start": v(15, -120) * mm, "mid": v(0, -135) * mm, "end": v(-15, -120) * mm});
            skLineSegment(sketch, "E89.MirrorCS", {"start": v(15, -108) * mm, "end": v(33, -90) * mm});
            skLineSegment(sketch, "E90.MirrorCS", {"start": v(0, -90) * mm, "end": v(0, -120) * mm, "construction": true});
            skCircle(sketch, "E91.MirrorC", {"center": v(0, -120) * mm, "radius": 6 * mm});
            skLineSegment(sketch, "E92.MirrorCS", {"start": v(15, -120) * mm, "end": v(15, -108) * mm});
            skLineSegment(sketch, "E93.MirrorCS", {"start": v(-15, -120) * mm, "end": v(-15, -108) * mm});
            skSolve(sketch);
        }
        {
            var Q0;
            Q0=makeQuery(id+"F16.imprint","IMPRINT",FACE,{"disambiguationData":[TD([[makeQuery(id+"F16.imprint","IMPRINT",EDGE,{"derivedFrom":sQuery(id+"F16.wireOp",EDGE,"E88.MirrorCS")}),-1.0]])]});
            var Q1;
            Q1=makeQuery(id+"F16.imprint","IMPRINT",FACE,{"disambiguationData":[TD([[makeQuery(id+"F16.imprint","IMPRINT",EDGE,{"derivedFrom":makeQuery(id+"F1.opExtrude","CAP_EDGE",EDGE,{"disambiguationData":[OSD([sQuery(id+"F0.wireOp",EDGE,"E1.left")])],"isStart":true})}),-1.0]])]});
            var Q2;
            Q2=makeQuery(id+"F16.imprint","IMPRINT",FACE,{"disambiguationData":[TD([[makeQuery(id+"F16.imprint","IMPRINT",EDGE,{"derivedFrom":sQuery(id+"F16.wireOp",EDGE,"E80")}),-1.0]])]});
            var Q3;
            Q3=makeQuery(id+"F2.opExtrude","CAP_FACE",FACE,{"disambiguationData":[OSD([sQuery(id+"F0.wireOp",EDGE,"E12"),sQuery(id+"F0.wireOp",EDGE,"E13"),sQuery(id+"F0.wireOp",EDGE,"E14"),sQuery(id+"F0.wireOp",EDGE,"E15"),sQuery(id+"F0.wireOp",EDGE,"E17.filletArc"),sQuery(id+"F0.wireOp",EDGE,"E18.filletArc"),sQuery(id+"F0.wireOp",EDGE,"E19.filletArc"),sQuery(id+"F0.wireOp",EDGE,"E20.filletArc"),sQuery(id+"F0.wireOp",EDGE,"E25.0"),sQuery(id+"F0.wireOp",EDGE,"E25.1"),sQuery(id+"F0.wireOp",EDGE,"E25.2"),sQuery(id+"F0.wireOp",EDGE,"E25.3"),sQuery(id+"F0.wireOp",EDGE,"E25.4"),sQuery(id+"F0.wireOp",EDGE,"E25.5"),sQuery(id+"F0.wireOp",EDGE,"E25.6"),sQuery(id+"F0.wireOp",EDGE,"E25.7")])],"isStart":false});
            extrude(context, id + "F17", {"entities" : qUnion([Q0, Q1, Q2]), "operationType" : NewBodyOperationType.ADD, "endBound" : BoundingType.UP_TO_SURFACE, "depth" : 25 * mm, "endBoundEntityFace" : qUnion([Q3]), "offsetDistance" : 25 * mm});
        }
    });
